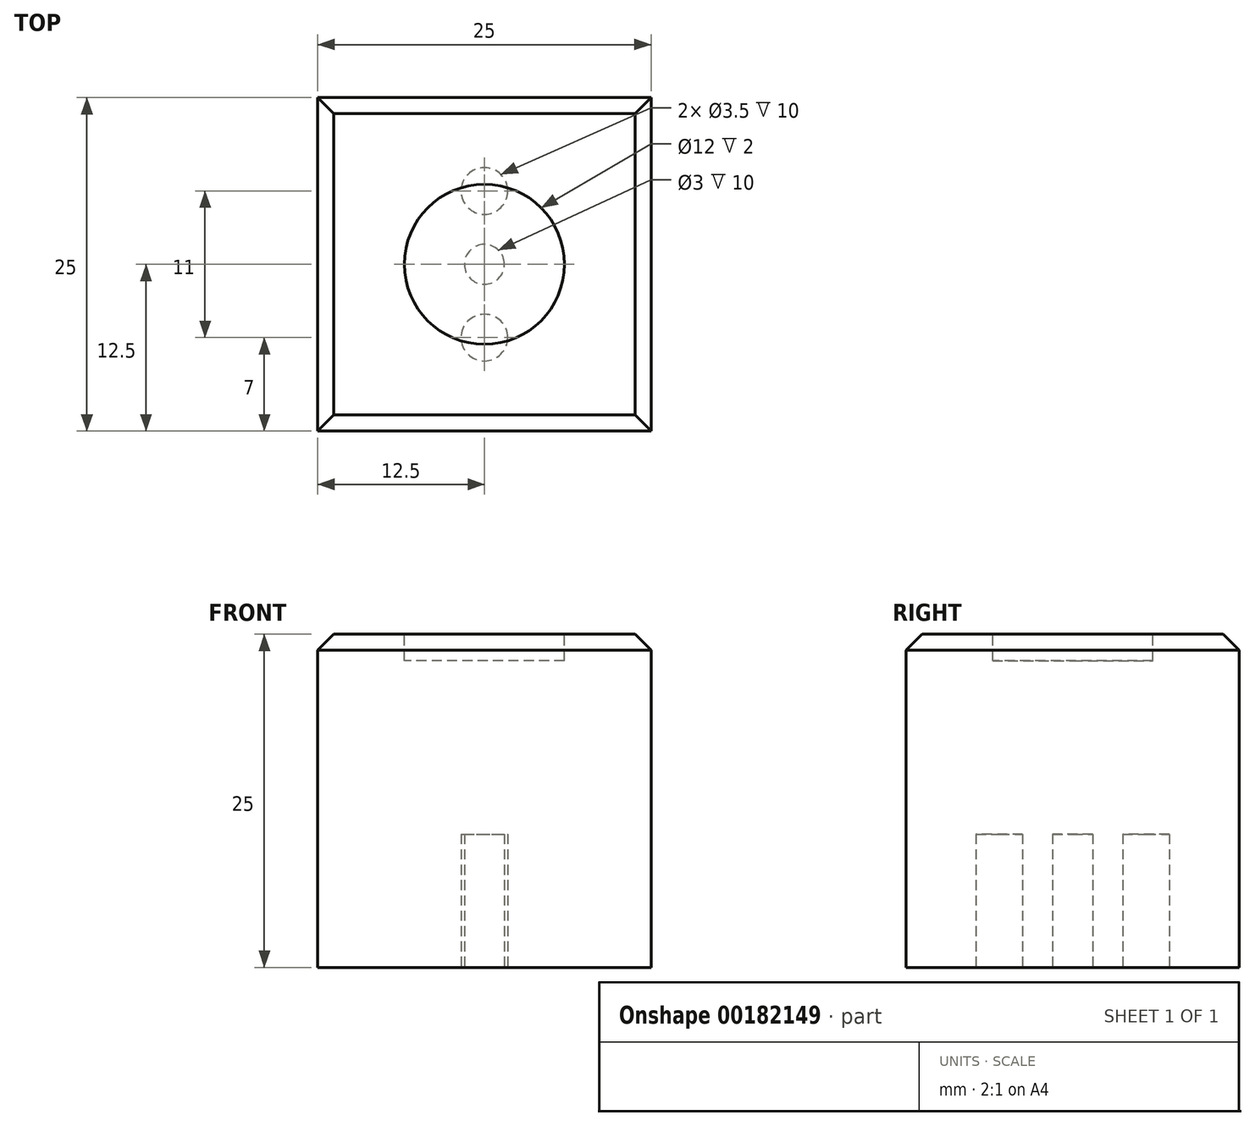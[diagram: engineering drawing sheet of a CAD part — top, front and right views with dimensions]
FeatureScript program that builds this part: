
annotation { "Feature Type Name" : "Feature", "Feature Type Description" : "" }
export const myFeature = defineFeature(function(context is Context, id is Id, definition is map)
    precondition{}
    {
        {
            var Q0;
            Q0=qCreatedBy(makeId("Top.planeOp"),FACE);
            var sketch = newSketch(context, id + "F0", { "sketchPlane" : qUnion([Q0])});
            skLineSegment(sketch, "E0.bottom", {"start": v(12.5, -12.5) * mm, "end": v(-12.5, -12.5) * mm});
            skLineSegment(sketch, "E0.top", {"start": v(12.5, 12.5) * mm, "end": v(-12.5, 12.5) * mm});
            skLineSegment(sketch, "E0.left", {"start": v(12.5, -12.5) * mm, "end": v(12.5, 12.5) * mm});
            skLineSegment(sketch, "E0.right", {"start": v(-12.5, -12.5) * mm, "end": v(-12.5, 12.5) * mm});
            skPoint(sketch, "E0.middle", {"position": v(0, 0) * mm});
            skSolve(sketch);
        }
        {
            var Q0;
            Q0 = qSketchRegion(id + "F0", true);
            extrude(context, id + "F1", {"entities" : qUnion([Q0]), "depth" : 25 * mm});
        }
        {
            var Q0;
            Q0=makeQuery(id+"F1.opExtrude","CAP_FACE",FACE,{"disambiguationData":[OSD([sQuery(id+"F0.wireOp",EDGE,"E0.bottom"),sQuery(id+"F0.wireOp",EDGE,"E0.top"),sQuery(id+"F0.wireOp",EDGE,"E0.left"),sQuery(id+"F0.wireOp",EDGE,"E0.right")])],"isStart":false});
            var sketch = newSketch(context, id + "F2", { "sketchPlane" : qUnion([Q0])});
            skCircle(sketch, "E1", {"center": v(0, 0) * mm, "radius": 6 * mm});
            skSolve(sketch);
        }
        {
            var Q0;
            Q0 = qSketchRegion(id + "F2", true);
            extrude(context, id + "F3", {"entities" : qUnion([Q0]), "operationType" : NewBodyOperationType.REMOVE, "oppositeDirection" : true, "depth" : 2 * mm});
        }
        {
            var Q0;
            Q0=makeQuery(id+"F1.opExtrude","CAP_FACE",FACE,{"disambiguationData":[OSD([sQuery(id+"F0.wireOp",EDGE,"E0.bottom"),sQuery(id+"F0.wireOp",EDGE,"E0.top"),sQuery(id+"F0.wireOp",EDGE,"E0.left"),sQuery(id+"F0.wireOp",EDGE,"E0.right")])],"isStart":true});
            var sketch = newSketch(context, id + "F4", { "sketchPlane" : qUnion([Q0])});
            skLineSegment(sketch, "E2", {"start": v(0, -12.5) * mm, "end": v(0, 12.5) * mm});
            skCircle(sketch, "E3", {"center": v(0, 0) * mm, "radius": 1.5 * mm});
            skCircle(sketch, "E4", {"center": v(0, 5.5) * mm, "radius": 1.75 * mm});
            skCircle(sketch, "E5", {"center": v(0, -5.5) * mm, "radius": 1.75 * mm});
            skSolve(sketch);
        }
        {
            var Q0;
            Q0 = qSketchRegion(id + "F4", true);
            extrude(context, id + "F5", {"entities" : qUnion([Q0]), "operationType" : NewBodyOperationType.REMOVE, "oppositeDirection" : true, "depth" : 10 * mm});
        }
        {
            var Q0;
            Q0=makeQuery(id+"F1.opExtrude","CAP_EDGE",EDGE,{"disambiguationData":[OSD([sQuery(id+"F0.wireOp",EDGE,"E0.top")])],"isStart":false});
            var Q1;
            Q1=makeQuery(id+"F1.opExtrude","CAP_EDGE",EDGE,{"disambiguationData":[OSD([sQuery(id+"F0.wireOp",EDGE,"E0.right")])],"isStart":false});
            var Q2;
            Q2=makeQuery(id+"F1.opExtrude","CAP_EDGE",EDGE,{"disambiguationData":[OSD([sQuery(id+"F0.wireOp",EDGE,"E0.bottom")])],"isStart":false});
            var Q3;
            Q3=makeQuery(id+"F1.opExtrude","CAP_EDGE",EDGE,{"disambiguationData":[OSD([sQuery(id+"F0.wireOp",EDGE,"E0.left")])],"isStart":false});
            chamfer(context, id + "F6", {"entities" : qUnion([Q0, Q1, Q2, Q3]), "width" : 1.2 * mm, "tangentPropagation" : true});
        }
    });
